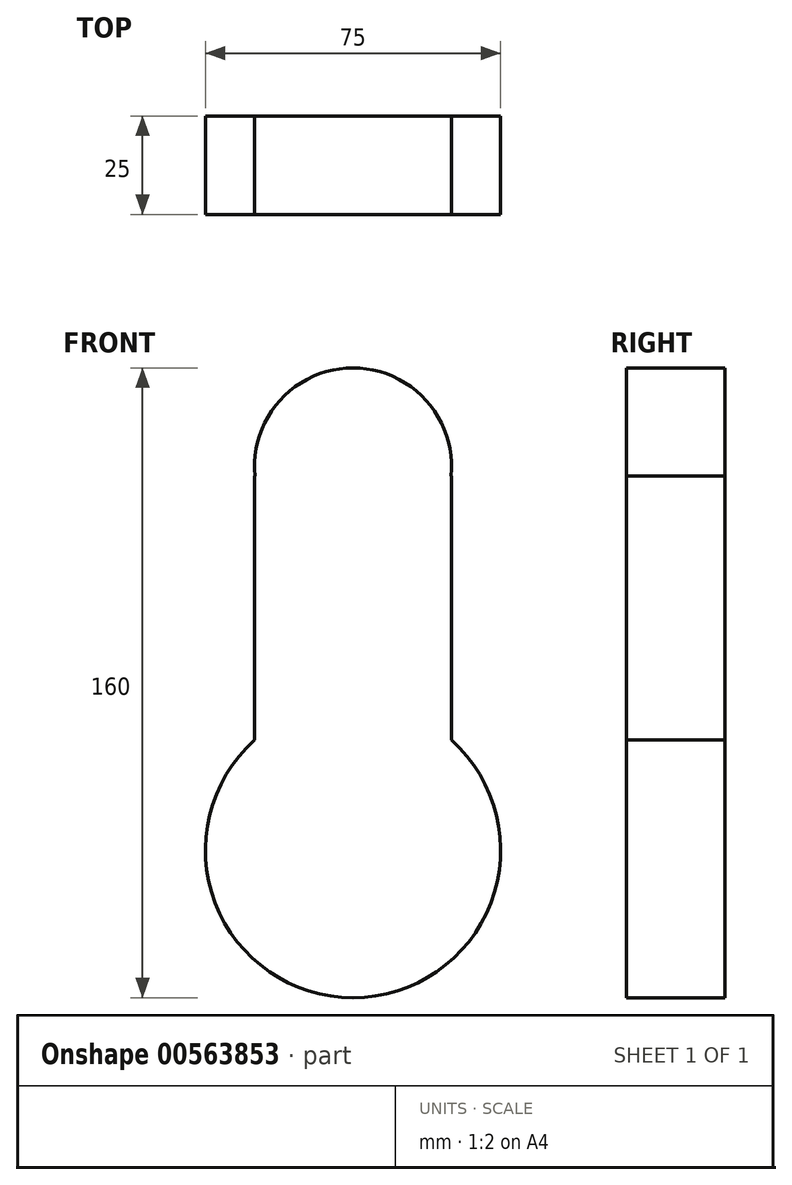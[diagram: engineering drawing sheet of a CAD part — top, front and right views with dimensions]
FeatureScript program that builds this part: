
annotation { "Feature Type Name" : "Feature", "Feature Type Description" : "" }
export const myFeature = defineFeature(function(context is Context, id is Id, definition is map)
    precondition{}
    {
        {
            var Q0;
            Q0=qCreatedBy(makeId("Front.planeOp"),FACE);
            var sketch = newSketch(context, id + "F0", { "sketchPlane" : qUnion([Q0])});
            skCircle(sketch, "E0", {"center": v(0, 40) * mm, "radius": 25 * mm});
            skCircle(sketch, "E1", {"center": v(0, -57.5) * mm, "radius": 37.5 * mm});
            skLineSegment(sketch, "E2.bottom", {"start": v(25, -37.5) * mm, "end": v(-25, -37.5) * mm});
            skLineSegment(sketch, "E2.top", {"start": v(25, 37.5) * mm, "end": v(-25, 37.5) * mm});
            skLineSegment(sketch, "E2.left", {"start": v(25, -37.5) * mm, "end": v(25, 37.5) * mm});
            skLineSegment(sketch, "E2.right", {"start": v(-25, -37.5) * mm, "end": v(-25, 37.5) * mm});
            skPoint(sketch, "E2.middle", {"position": v(0, 0) * mm});
            skSolve(sketch);
        }
        {
            var Q0;
            Q0 = qSketchRegion(id + "F0", true);
            extrude(context, id + "F1", {"entities" : qUnion([Q0]), "depth" : 25 * mm, "offsetDistance" : 25 * mm});
        }
    });
